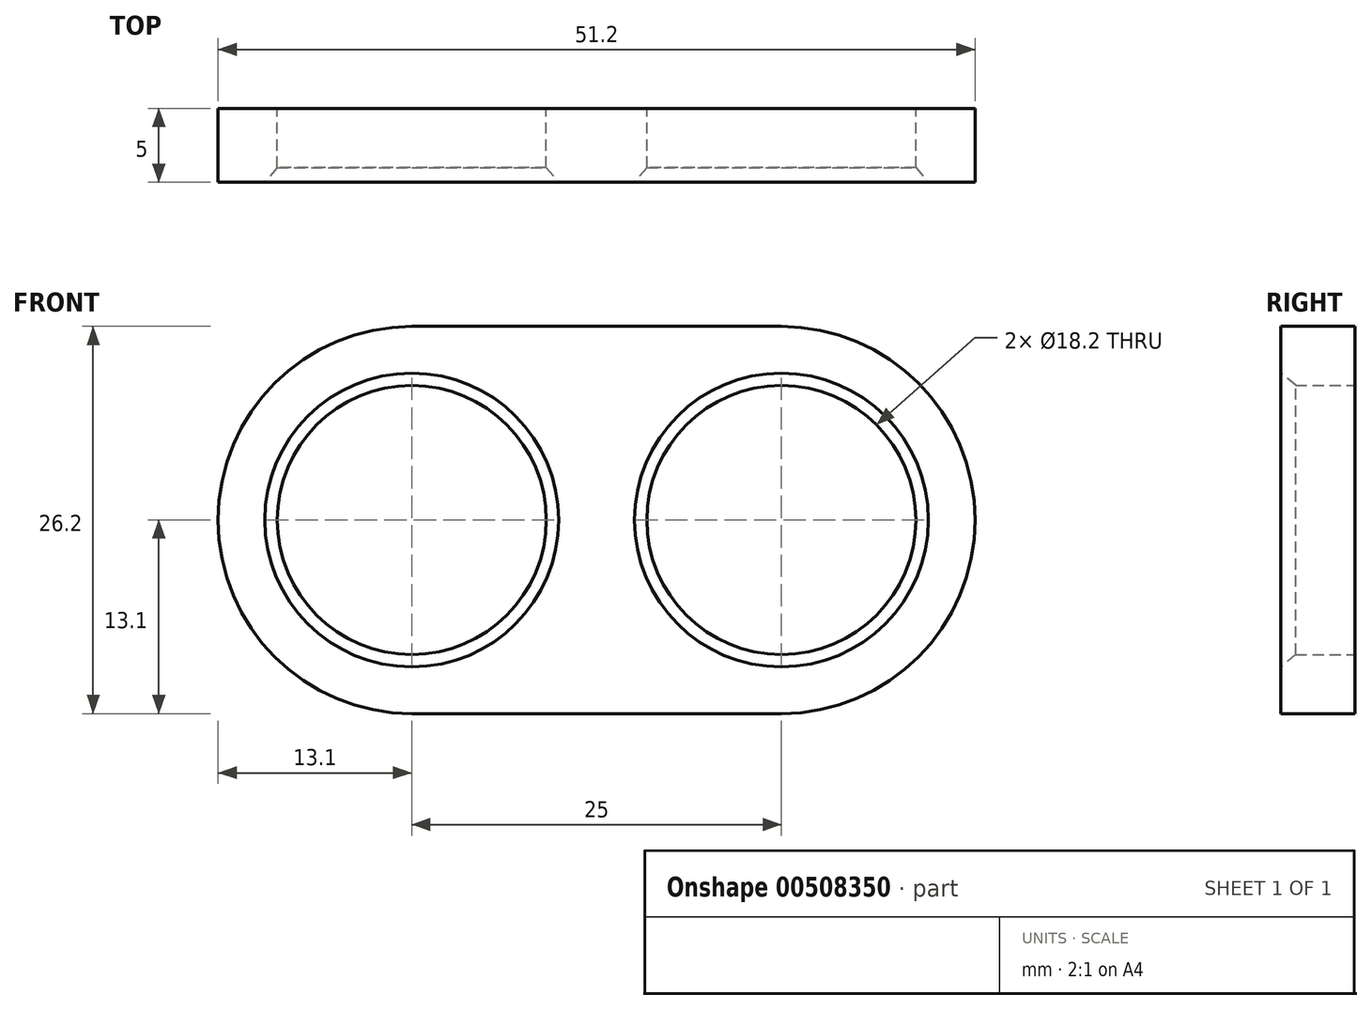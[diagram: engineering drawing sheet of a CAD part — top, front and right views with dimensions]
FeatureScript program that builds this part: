
annotation { "Feature Type Name" : "Feature", "Feature Type Description" : "" }
export const myFeature = defineFeature(function(context is Context, id is Id, definition is map)
    precondition{}
    {
        {
            var Q0;
            Q0=qCreatedBy(makeId("Front.planeOp"),FACE);
            var sketch = newSketch(context, id + "F0", { "sketchPlane" : qUnion([Q0])});
            skCircle(sketch, "E0", {"center": v(0, 0) * mm, "radius": 9.1 * mm});
            skCircle(sketch, "E1", {"center": v(25, 0) * mm, "radius": 9.1 * mm});
            skLineSegment(sketch, "E2", {"start": v(0, 0) * mm, "end": v(25, 0) * mm, "construction": true});
            skLineSegment(sketch, "E3", {"start": v(12.5, 0) * mm, "end": v(12.5, 4.25) * mm, "construction": true});
            skArc(sketch, "E4", {"start": v(0, 13.1) * mm, "mid": v(-13.1, 0) * mm, "end": v(0, -13.1) * mm});
            skArc(sketch, "E5.MirrorC", {"start": v(25, 13.1) * mm, "mid": v(38.1, 0) * mm, "end": v(25, -13.1) * mm});
            skLineSegment(sketch, "E6", {"start": v(0, 13.1) * mm, "end": v(25, 13.1) * mm});
            skLineSegment(sketch, "E7.MirrorCS", {"start": v(0, -13.1) * mm, "end": v(25, -13.1) * mm});
            skPoint(sketch, "E8.orphan", {"position": v(-5.4, 13.1) * mm});
            skPoint(sketch, "E9.orphan", {"position": v(-5.4, -13.1) * mm});
            skPoint(sketch, "E10.orphan", {"position": v(37.86, -13.1) * mm});
            skPoint(sketch, "E11.orphan", {"position": v(37.86, 13.1) * mm});
            skSolve(sketch);
        }
        {
            var Q0;
            Q0=makeQuery(id+"F0.imprint","IMPRINT",FACE,{"disambiguationData":[TD([[makeQuery(id+"F0.imprint","IMPRINT",EDGE,{"derivedFrom":sQuery(id+"F0.wireOp",EDGE,"E0")}),-1.0]])]});
            extrude(context, id + "F1", {"entities" : qUnion([Q0]), "depth" : 5 * mm, "offsetDistance" : 25 * mm});
        }
        {
            var Q0;
            Q0=makeQuery(id+"F1.opExtrude","CAP_EDGE",EDGE,{"disambiguationData":[OSD([sQuery(id+"F0.wireOp",EDGE,"E0")])],"isStart":false});
            var Q1;
            Q1=makeQuery(id+"F1.opExtrude","CAP_EDGE",EDGE,{"disambiguationData":[OSD([sQuery(id+"F0.wireOp",EDGE,"E1")])],"isStart":false});
            chamfer(context, id + "F2", {"entities" : qUnion([Q0, Q1]), "chamferType" : ChamferType.OFFSET_ANGLE, "width" : 1 * mm, "oppositeDirection" : false, "angle" : 40 * degree, "tangentPropagation" : true});
        }
    });
